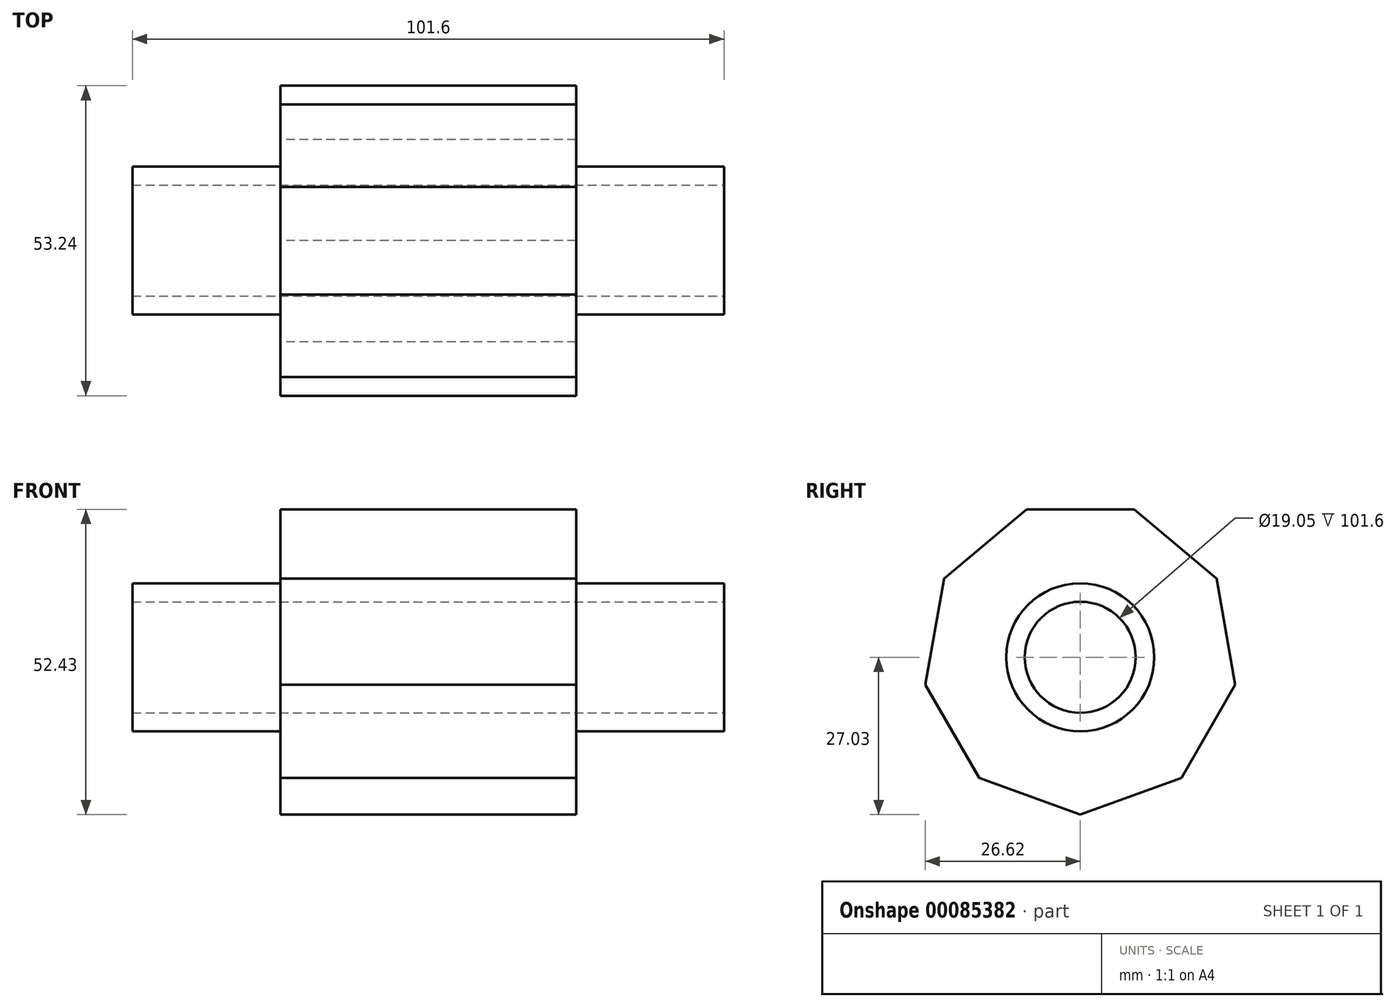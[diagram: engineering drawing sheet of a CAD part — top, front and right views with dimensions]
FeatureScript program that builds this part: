
annotation { "Feature Type Name" : "Feature", "Feature Type Description" : "" }
export const myFeature = defineFeature(function(context is Context, id is Id, definition is map)
    precondition{}
    {
        {
            var Q0;
            Q0=qCreatedBy(makeId("Right.planeOp"),FACE);
            var sketch = newSketch(context, id + "F0", { "sketchPlane" : qUnion([Q0])});
            skCircle(sketch, "E0.cCircle", {"center": v(0, 0) * mm, "radius": 25.4 * mm, "construction": true});
            skLineSegment(sketch, "E0.0", {"start": v(-9.24, 25.4) * mm, "end": v(9.24, 25.4) * mm});
            skLineSegment(sketch, "E0.1", {"start": v(9.24, 25.4) * mm, "end": v(23.4, 13.52) * mm});
            skLineSegment(sketch, "E0.2", {"start": v(23.4, 13.52) * mm, "end": v(26.62, -4.7) * mm});
            skLineSegment(sketch, "E0.3", {"start": v(26.62, -4.7) * mm, "end": v(17.37, -20.7) * mm});
            skLineSegment(sketch, "E0.4", {"start": v(17.37, -20.7) * mm, "end": v(0, -27.03) * mm});
            skLineSegment(sketch, "E0.5", {"start": v(0, -27.03) * mm, "end": v(-17.37, -20.7) * mm});
            skLineSegment(sketch, "E0.6", {"start": v(-17.37, -20.7) * mm, "end": v(-26.62, -4.7) * mm});
            skLineSegment(sketch, "E0.7", {"start": v(-26.62, -4.7) * mm, "end": v(-23.4, 13.52) * mm});
            skLineSegment(sketch, "E0.8", {"start": v(-23.4, 13.52) * mm, "end": v(-9.24, 25.4) * mm});
            skPoint(sketch, "E0.0.midPoint", {"position": v(0, 25.4) * mm});
            skSolve(sketch);
        }
        {
            var Q0;
            Q0=makeQuery(id+"F0.imprint","IMPRINT",FACE,{"disambiguationData":[TD([[makeQuery(id+"F0.imprint","IMPRINT",EDGE,{"derivedFrom":sQuery(id+"F0.wireOp",EDGE,"E0.0")}),-1.0]])]});
            extrude(context, id + "F1", {"entities" : qUnion([Q0]), "depth" : 50.8 * mm});
        }
        {
            var Q0;
            Q0=makeQuery(id+"F1.opExtrude","CAP_FACE",FACE,{"disambiguationData":[OSD([sQuery(id+"F0.wireOp",EDGE,"E0.0"),sQuery(id+"F0.wireOp",EDGE,"E0.1"),sQuery(id+"F0.wireOp",EDGE,"E0.2"),sQuery(id+"F0.wireOp",EDGE,"E0.3"),sQuery(id+"F0.wireOp",EDGE,"E0.4"),sQuery(id+"F0.wireOp",EDGE,"E0.5"),sQuery(id+"F0.wireOp",EDGE,"E0.6"),sQuery(id+"F0.wireOp",EDGE,"E0.7"),sQuery(id+"F0.wireOp",EDGE,"E0.8")])],"isStart":false});
            var sketch = newSketch(context, id + "F2", { "sketchPlane" : qUnion([Q0])});
            skCircle(sketch, "E1", {"center": v(0, 0) * mm, "radius": 12.7 * mm});
            skSolve(sketch);
        }
        {
            var Q0;
            Q0=makeQuery(id+"F2.imprint","IMPRINT",FACE,{"disambiguationData":[TD([[makeQuery(id+"F2.imprint","IMPRINT",EDGE,{"derivedFrom":sQuery(id+"F2.wireOp",EDGE,"E1")}),1.0]])]});
            extrude(context, id + "F3", {"entities" : qUnion([Q0]), "operationType" : NewBodyOperationType.ADD, "depth" : 25.4 * mm});
        }
        {
            var Q0;
            Q0=makeQuery(id+"F3.opExtrude","CAP_FACE",FACE,{"disambiguationData":[OSD([sQuery(id+"F2.wireOp",EDGE,"E1")])],"isStart":false});
            var sketch = newSketch(context, id + "F4", { "sketchPlane" : qUnion([Q0])});
            skCircle(sketch, "E2", {"center": v(0, 0) * mm, "radius": 9.53 * mm});
            skSolve(sketch);
        }
        {
            var Q0;
            Q0=makeQuery(id+"F4.imprint","IMPRINT",FACE,{"disambiguationData":[TD([[makeQuery(id+"F4.imprint","IMPRINT",EDGE,{"derivedFrom":sQuery(id+"F4.wireOp",EDGE,"E2")}),1.0]])]});
            extrude(context, id + "F5", {"entities" : qUnion([Q0]), "operationType" : NewBodyOperationType.REMOVE, "oppositeDirection" : true, "depth" : 76.2 * mm});
        }
        {
            var Q0;
            Q0=makeQuery(id+"F1.opExtrude","CAP_FACE",FACE,{"disambiguationData":[OSD([sQuery(id+"F0.wireOp",EDGE,"E0.0"),sQuery(id+"F0.wireOp",EDGE,"E0.1"),sQuery(id+"F0.wireOp",EDGE,"E0.2"),sQuery(id+"F0.wireOp",EDGE,"E0.3"),sQuery(id+"F0.wireOp",EDGE,"E0.4"),sQuery(id+"F0.wireOp",EDGE,"E0.5"),sQuery(id+"F0.wireOp",EDGE,"E0.6"),sQuery(id+"F0.wireOp",EDGE,"E0.7"),sQuery(id+"F0.wireOp",EDGE,"E0.8")])],"isStart":true});
            var sketch = newSketch(context, id + "F6", { "sketchPlane" : qUnion([Q0])});
            skCircle(sketch, "E3", {"center": v(0, 0) * mm, "radius": 12.7 * mm});
            skSolve(sketch);
        }
        {
            var Q0;
            Q0=makeQuery(id+"F6.imprint","IMPRINT",FACE,{"disambiguationData":[TD([[makeQuery(id+"F6.imprint","IMPRINT",EDGE,{"derivedFrom":sQuery(id+"F6.wireOp",EDGE,"E3")}),1.0]])]});
            extrude(context, id + "F7", {"entities" : qUnion([Q0]), "operationType" : NewBodyOperationType.ADD, "depth" : 25.4 * mm});
        }
    });
